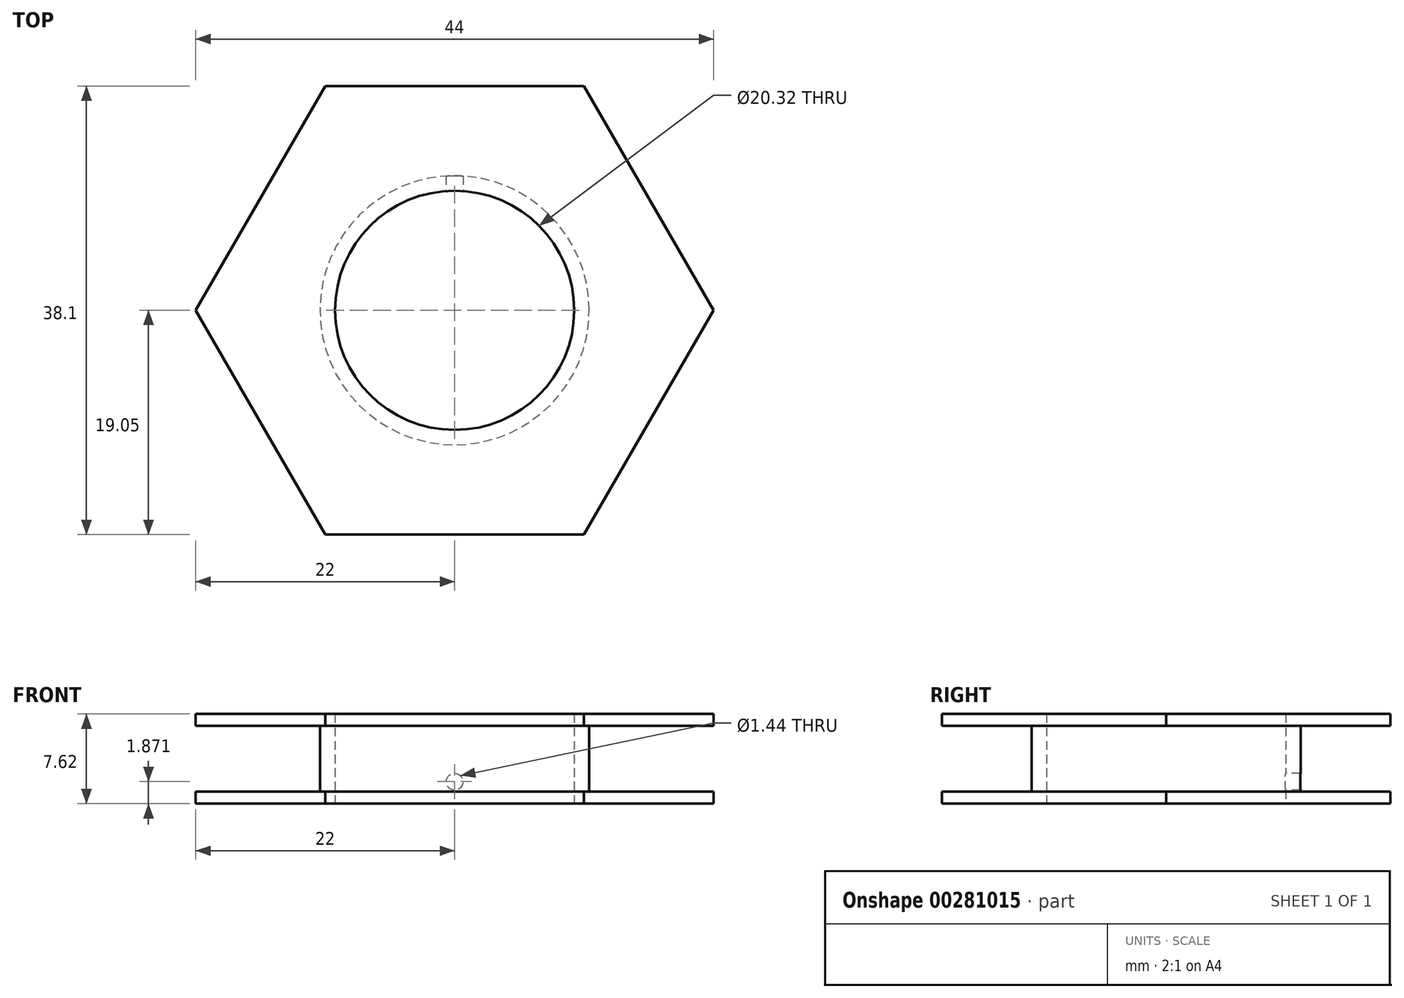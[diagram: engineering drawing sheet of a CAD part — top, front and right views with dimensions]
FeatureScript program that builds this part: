
annotation { "Feature Type Name" : "Feature", "Feature Type Description" : "" }
export const myFeature = defineFeature(function(context is Context, id is Id, definition is map)
    precondition{}
    {
        {
            var Q0;
            Q0=qCreatedBy(makeId("Top.planeOp"),FACE);
            var sketch = newSketch(context, id + "F0", { "sketchPlane" : qUnion([Q0])});
            skCircle(sketch, "E0.cCircle", {"center": v(0, 0) * mm, "radius": 19.05 * mm, "construction": true});
            skLineSegment(sketch, "E0.0", {"start": v(-11, 19.05) * mm, "end": v(11, 19.05) * mm});
            skLineSegment(sketch, "E0.1", {"start": v(11, 19.05) * mm, "end": v(22, 0) * mm});
            skLineSegment(sketch, "E0.2", {"start": v(22, 0) * mm, "end": v(11, -19.05) * mm});
            skLineSegment(sketch, "E0.3", {"start": v(11, -19.05) * mm, "end": v(-11, -19.05) * mm});
            skLineSegment(sketch, "E0.4", {"start": v(-11, -19.05) * mm, "end": v(-22, 0) * mm});
            skLineSegment(sketch, "E0.5", {"start": v(-22, 0) * mm, "end": v(-11, 19.05) * mm});
            skPoint(sketch, "E0.0.midPoint", {"position": v(0, 19.05) * mm});
            skSolve(sketch);
        }
        {
            var Q0;
            Q0 = qSketchRegion(id + "F0", true);
            extrude(context, id + "F1", {"entities" : qUnion([Q0]), "depth" : 7.62 * mm});
        }
        {
            var Q0;
            Q0=makeQuery(id+"F1.opExtrude","CAP_FACE",FACE,{"disambiguationData":[OSD([sQuery(id+"F0.wireOp",EDGE,"E0.0"),sQuery(id+"F0.wireOp",EDGE,"E0.1"),sQuery(id+"F0.wireOp",EDGE,"E0.2"),sQuery(id+"F0.wireOp",EDGE,"E0.3"),sQuery(id+"F0.wireOp",EDGE,"E0.4"),sQuery(id+"F0.wireOp",EDGE,"E0.5")])],"isStart":true});
            var sketch = newSketch(context, id + "F2", { "sketchPlane" : qUnion([Q0])});
            skCircle(sketch, "E1", {"center": v(0, 0) * mm, "radius": 12.7 * mm});
            skCircle(sketch, "E2", {"center": v(0, 0) * mm, "radius": 10.16 * mm});
            skSolve(sketch);
        }
        {
            var Q0;
            Q0=makeQuery(id+"F2.imprint","IMPRINT",FACE,{"disambiguationData":[TD([[makeQuery(id+"F2.imprint","IMPRINT",EDGE,{"derivedFrom":sQuery(id+"F2.wireOp",EDGE,"E2")}),1.0]])]});
            extrude(context, id + "F3", {"entities" : qUnion([Q0]), "operationType" : NewBodyOperationType.REMOVE, "oppositeDirection" : true, "depth" : 25.4 * mm});
        }
        {
            var Q0;
            Q0=qCreatedBy(makeId("Top.planeOp"),FACE);
            cPlane(context, id + "F4", {"entities" : qUnion([Q0]), "cplaneType" : CPlaneType.OFFSET, "offset" : 1.02 * mm, "width" : 152.4 * mm, "height" : 152.4 * mm});
        }
        {
            var Q0;
            Q0=qCreatedBy(id+"F4.planeOp",FACE);
            var sketch = newSketch(context, id + "F5", { "sketchPlane" : qUnion([Q0])});
            skLineSegment(sketch, "E3.1", {"start": v(22, 0) * mm, "end": v(11, -19.05) * mm});
            skLineSegment(sketch, "E3.2", {"start": v(11, -19.05) * mm, "end": v(-11, -19.05) * mm});
            skLineSegment(sketch, "E3.3", {"start": v(-11, -19.05) * mm, "end": v(-22, 0) * mm});
            skLineSegment(sketch, "E3.4", {"start": v(-11, 19.05) * mm, "end": v(11, 19.05) * mm});
            skLineSegment(sketch, "E3.5", {"start": v(11, 19.05) * mm, "end": v(22, 0) * mm});
            skLineSegment(sketch, "E4.5", {"start": v(-22, 0) * mm, "end": v(-11, 19.05) * mm});
            skCircle(sketch, "E5", {"center": v(0, 0) * mm, "radius": 11.43 * mm});
            skSolve(sketch);
        }
        {
            var Q0;
            Q0 = qSketchRegion(id + "F5", true);
            extrude(context, id + "F6", {"entities" : qUnion([Q0]), "operationType" : NewBodyOperationType.REMOVE, "depth" : 5.6 * mm});
        }
        {
            var Q0;
            Q0=qCreatedBy(makeId("Front.planeOp"),FACE);
            var sketch = newSketch(context, id + "F7", { "sketchPlane" : qUnion([Q0])});
            skCircle(sketch, "E6", {"center": v(0, 1.87) * mm, "radius": 0.72 * mm});
            skSolve(sketch);
        }
        {
            var Q0;
            Q0 = qSketchRegion(id + "F7", true);
            extrude(context, id + "F8", {"entities" : qUnion([Q0]), "operationType" : NewBodyOperationType.REMOVE, "oppositeDirection" : true, "depth" : 25.4 * mm});
        }
    });
